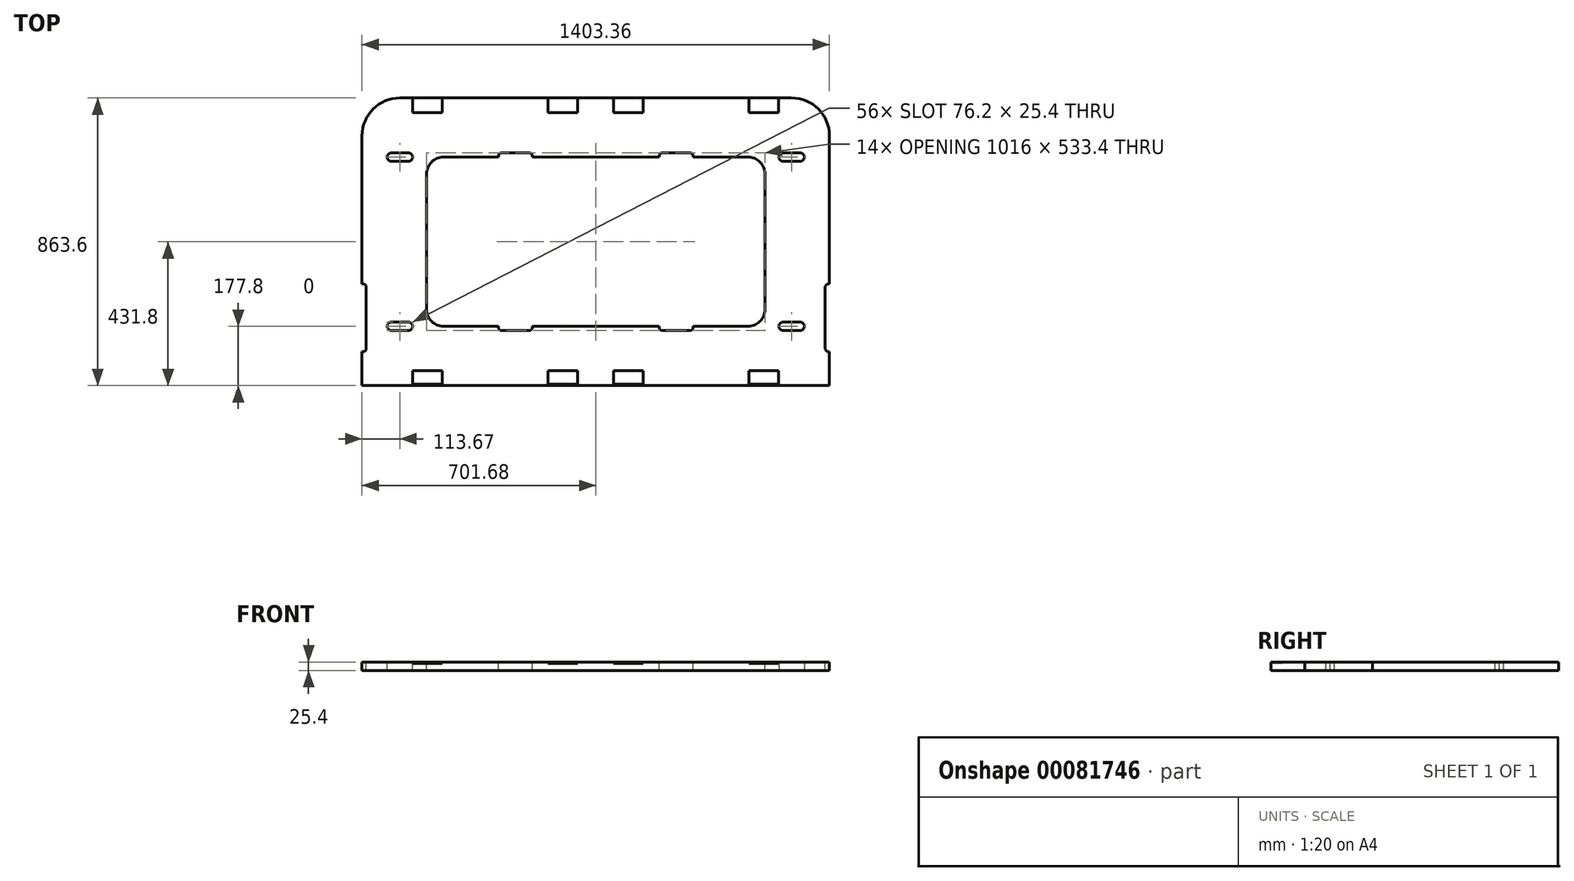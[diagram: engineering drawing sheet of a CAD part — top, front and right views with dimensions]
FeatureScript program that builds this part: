
annotation { "Feature Type Name" : "Feature", "Feature Type Description" : "" }
export const myFeature = defineFeature(function(context is Context, id is Id, definition is map)
    precondition{}
    {
        {
            var Q0;
            Q0=qCreatedBy(makeId("Top.planeOp"),FACE);
            var sketch = newSketch(context, id + "F0", { "sketchPlane" : qUnion([Q0])});
            skLineSegment(sketch, "E0.bottom", {"start": v(-701.68, -431.8) * mm, "end": v(701.68, -431.8) * mm});
            skLineSegment(sketch, "E0.top", {"start": v(-701.68, 431.8) * mm, "end": v(701.68, 431.8) * mm});
            skLineSegment(sketch, "E0.left", {"start": v(-701.68, -431.8) * mm, "end": v(-701.68, 431.8) * mm});
            skLineSegment(sketch, "E0.right", {"start": v(701.68, -431.8) * mm, "end": v(701.68, 431.8) * mm});
            skPoint(sketch, "E0.middle", {"position": v(0, 0) * mm});
            skSolve(sketch);
        }
        {
            var Q0;
            Q0=makeQuery(id+"F0.imprint","IMPRINT",FACE,{"disambiguationData":[TD([[makeQuery(id+"F0.imprint","IMPRINT",EDGE,{"derivedFrom":sQuery(id+"F0.wireOp",EDGE,"E0.bottom")}),1.0]])]});
            extrude(context, id + "F1", {"entities" : qUnion([Q0]), "depth" : 25.4 * mm, "offsetDistance" : 25.4 * mm});
        }
        {
            var Q0;
            Q0=makeQuery(id+"F1.opExtrude","CAP_FACE",FACE,{"disambiguationData":[OSD([sQuery(id+"F0.wireOp",EDGE,"E0.bottom"),sQuery(id+"F0.wireOp",EDGE,"E0.top"),sQuery(id+"F0.wireOp",EDGE,"E0.left"),sQuery(id+"F0.wireOp",EDGE,"E0.right")])],"isStart":false});
            var sketch = newSketch(context, id + "F2", { "sketchPlane" : qUnion([Q0])});
            skLineSegment(sketch, "E1.bottom", {"start": v(-457.2, 254) * mm, "end": v(457.2, 254) * mm});
            skLineSegment(sketch, "E1.top", {"start": v(-457.2, -254) * mm, "end": v(457.2, -254) * mm});
            skLineSegment(sketch, "E1.left", {"start": v(-508, 203.2) * mm, "end": v(-508, -203.2) * mm});
            skLineSegment(sketch, "E1.right", {"start": v(508, 203.2) * mm, "end": v(508, -203.2) * mm});
            skPoint(sketch, "E2.visualSharp", {"position": v(-508, 254) * mm});
            skArc(sketch, "E2.filletArc", {"start": v(-457.2, 254) * mm, "mid": v(-493.12, 239.12) * mm, "end": v(-508, 203.2) * mm});
            skPoint(sketch, "E3.visualSharp", {"position": v(508, 254) * mm});
            skArc(sketch, "E3.filletArc", {"start": v(508, 203.2) * mm, "mid": v(493.12, 239.12) * mm, "end": v(457.2, 254) * mm});
            skPoint(sketch, "E4.visualSharp", {"position": v(508, -254) * mm});
            skArc(sketch, "E4.filletArc", {"start": v(457.2, -254) * mm, "mid": v(493.12, -239.12) * mm, "end": v(508, -203.2) * mm});
            skPoint(sketch, "E5.visualSharp", {"position": v(-508, -254) * mm});
            skArc(sketch, "E5.filletArc", {"start": v(-508, -203.2) * mm, "mid": v(-493.12, -239.12) * mm, "end": v(-457.2, -254) * mm});
            skSolve(sketch);
        }
        {
            var Q0;
            Q0 = qSketchRegion(id + "F2", true);
            extrude(context, id + "F3", {"entities" : qUnion([Q0]), "operationType" : NewBodyOperationType.REMOVE, "oppositeDirection" : true, "depth" : 25.4 * mm});
        }
        {
            var Q0;
            Q0=makeQuery(id+"F1.opExtrude","CAP_FACE",FACE,{"disambiguationData":[OSD([sQuery(id+"F0.wireOp",EDGE,"E0.bottom"),sQuery(id+"F0.wireOp",EDGE,"E0.top"),sQuery(id+"F0.wireOp",EDGE,"E0.left"),sQuery(id+"F0.wireOp",EDGE,"E0.right")])],"isStart":false});
            var sketch = newSketch(context, id + "F4", { "sketchPlane" : qUnion([Q0])});
            skLineSegment(sketch, "E6.bottom", {"start": v(-549.27, -431.8) * mm, "end": v(-460.38, -431.8) * mm});
            skLineSegment(sketch, "E6.top", {"start": v(-549.27, -387.35) * mm, "end": v(-460.38, -387.35) * mm});
            skLineSegment(sketch, "E6.left", {"start": v(-549.27, -431.8) * mm, "end": v(-549.27, -387.35) * mm});
            skLineSegment(sketch, "E6.right", {"start": v(-460.37, -431.8) * mm, "end": v(-460.37, -387.35) * mm});
            skLineSegment(sketch, "E7.bottom", {"start": v(-142.87, -431.8) * mm, "end": v(-53.97, -431.8) * mm});
            skLineSegment(sketch, "E7.top", {"start": v(-142.87, -387.35) * mm, "end": v(-53.97, -387.35) * mm});
            skLineSegment(sketch, "E7.left", {"start": v(-142.87, -431.8) * mm, "end": v(-142.87, -387.35) * mm});
            skLineSegment(sketch, "E7.right", {"start": v(-53.97, -431.8) * mm, "end": v(-53.97, -387.35) * mm});
            skLineSegment(sketch, "E8.bottom", {"start": v(53.98, -431.8) * mm, "end": v(142.88, -431.8) * mm});
            skLineSegment(sketch, "E8.top", {"start": v(53.98, -387.35) * mm, "end": v(142.88, -387.35) * mm});
            skLineSegment(sketch, "E8.left", {"start": v(53.98, -431.8) * mm, "end": v(53.98, -387.35) * mm});
            skLineSegment(sketch, "E8.right", {"start": v(142.88, -431.8) * mm, "end": v(142.88, -387.35) * mm});
            skLineSegment(sketch, "E9.bottom", {"start": v(460.38, -431.8) * mm, "end": v(549.28, -431.8) * mm});
            skLineSegment(sketch, "E9.top", {"start": v(460.38, -387.35) * mm, "end": v(549.28, -387.35) * mm});
            skLineSegment(sketch, "E9.left", {"start": v(460.38, -431.8) * mm, "end": v(460.38, -387.35) * mm});
            skLineSegment(sketch, "E9.right", {"start": v(549.28, -431.8) * mm, "end": v(549.28, -387.35) * mm});
            skSolve(sketch);
        }
        {
            var Q0;
            Q0 = qSketchRegion(id + "F4", true);
            extrude(context, id + "F5", {"entities" : qUnion([Q0]), "operationType" : NewBodyOperationType.REMOVE, "oppositeDirection" : true, "depth" : 3.17 * mm});
        }
        {
            var Q0;
            Q0=makeQuery(id+"F1.opExtrude","CAP_FACE",FACE,{"disambiguationData":[OSD([sQuery(id+"F0.wireOp",EDGE,"E0.bottom"),sQuery(id+"F0.wireOp",EDGE,"E0.top"),sQuery(id+"F0.wireOp",EDGE,"E0.left"),sQuery(id+"F0.wireOp",EDGE,"E0.right")])],"isStart":false});
            var sketch = newSketch(context, id + "F6", { "sketchPlane" : qUnion([Q0])});
            skLineSegment(sketch, "E10.bottom", {"start": v(-549.27, -431.8) * mm, "end": v(-460.37, -431.8) * mm});
            skLineSegment(sketch, "E10.top", {"start": v(-549.27, -428) * mm, "end": v(-460.37, -428) * mm});
            skLineSegment(sketch, "E10.left", {"start": v(-549.27, -431.8) * mm, "end": v(-549.27, -428) * mm});
            skLineSegment(sketch, "E10.right", {"start": v(-460.37, -431.8) * mm, "end": v(-460.37, -428) * mm});
            skLineSegment(sketch, "E11.bottom", {"start": v(-142.87, -431.8) * mm, "end": v(-53.97, -431.8) * mm});
            skLineSegment(sketch, "E11.top", {"start": v(-142.87, -428) * mm, "end": v(-53.97, -428) * mm});
            skLineSegment(sketch, "E11.left", {"start": v(-142.87, -431.8) * mm, "end": v(-142.87, -428) * mm});
            skLineSegment(sketch, "E11.right", {"start": v(-53.97, -431.8) * mm, "end": v(-53.97, -428) * mm});
            skLineSegment(sketch, "E12.bottom", {"start": v(53.98, -431.8) * mm, "end": v(142.88, -431.8) * mm});
            skLineSegment(sketch, "E12.top", {"start": v(53.98, -428) * mm, "end": v(142.88, -428) * mm});
            skLineSegment(sketch, "E12.left", {"start": v(53.98, -431.8) * mm, "end": v(53.98, -428) * mm});
            skLineSegment(sketch, "E12.right", {"start": v(142.88, -431.8) * mm, "end": v(142.88, -428) * mm});
            skLineSegment(sketch, "E13.bottom", {"start": v(460.38, -431.8) * mm, "end": v(549.28, -431.8) * mm});
            skLineSegment(sketch, "E13.top", {"start": v(460.38, -428) * mm, "end": v(549.28, -428) * mm});
            skLineSegment(sketch, "E13.left", {"start": v(460.38, -431.8) * mm, "end": v(460.38, -428) * mm});
            skLineSegment(sketch, "E13.right", {"start": v(549.28, -431.8) * mm, "end": v(549.28, -428) * mm});
            skSolve(sketch);
        }
        {
            var Q0;
            Q0 = qSketchRegion(id + "F6", true);
            extrude(context, id + "F7", {"entities" : qUnion([Q0]), "operationType" : NewBodyOperationType.REMOVE, "oppositeDirection" : true, "depth" : 4.44 * mm});
        }
        {
            var Q0;
            Q0=makeQuery(id+"F1.opExtrude","SWEPT_EDGE",EDGE,{"disambiguationData":[OSD([sQuery(id+"F0.wireOp",EDGE,"E0.top"),sQuery(id+"F0.wireOp",EDGE,"E0.right")])]});
            var Q1;
            Q1=makeQuery(id+"F1.opExtrude","SWEPT_EDGE",EDGE,{"disambiguationData":[OSD([sQuery(id+"F0.wireOp",EDGE,"E0.top"),sQuery(id+"F0.wireOp",EDGE,"E0.left")])]});
            fillet(context, id + "F8", {"entities" : qUnion([Q0, Q1]), "radius" : 114.3 * mm, "tangentPropagation" : true, "allowEdgeOverflow" : false});
        }
        {
            var Q0;
            Q0=makeQuery(id+"F1.opExtrude","CAP_FACE",FACE,{"disambiguationData":[OSD([sQuery(id+"F0.wireOp",EDGE,"E0.bottom"),sQuery(id+"F0.wireOp",EDGE,"E0.top"),sQuery(id+"F0.wireOp",EDGE,"E0.left"),sQuery(id+"F0.wireOp",EDGE,"E0.right")])],"isStart":false});
            var sketch = newSketch(context, id + "F9", { "sketchPlane" : qUnion([Q0])});
            skLineSegment(sketch, "E14.bottom", {"start": v(53.97, 431.8) * mm, "end": v(142.88, 431.8) * mm});
            skLineSegment(sketch, "E14.top", {"start": v(53.97, 387.35) * mm, "end": v(142.88, 387.35) * mm});
            skLineSegment(sketch, "E14.left", {"start": v(53.97, 431.8) * mm, "end": v(53.97, 387.35) * mm});
            skLineSegment(sketch, "E14.right", {"start": v(142.87, 431.8) * mm, "end": v(142.87, 387.35) * mm});
            skLineSegment(sketch, "E15.bottom", {"start": v(460.38, 431.8) * mm, "end": v(549.28, 431.8) * mm});
            skLineSegment(sketch, "E15.top", {"start": v(460.38, 387.35) * mm, "end": v(549.28, 387.35) * mm});
            skLineSegment(sketch, "E15.left", {"start": v(460.38, 431.8) * mm, "end": v(460.38, 387.35) * mm});
            skLineSegment(sketch, "E15.right", {"start": v(549.28, 431.8) * mm, "end": v(549.28, 387.35) * mm});
            skLineSegment(sketch, "E16.bottom", {"start": v(-53.98, 431.8) * mm, "end": v(-142.88, 431.8) * mm});
            skLineSegment(sketch, "E16.top", {"start": v(-53.98, 387.35) * mm, "end": v(-142.88, 387.35) * mm});
            skLineSegment(sketch, "E16.left", {"start": v(-53.98, 431.8) * mm, "end": v(-53.98, 387.35) * mm});
            skLineSegment(sketch, "E16.right", {"start": v(-142.88, 431.8) * mm, "end": v(-142.88, 387.35) * mm});
            skLineSegment(sketch, "E17.bottom", {"start": v(-460.38, 431.8) * mm, "end": v(-549.28, 431.8) * mm});
            skLineSegment(sketch, "E17.top", {"start": v(-460.38, 387.35) * mm, "end": v(-549.28, 387.35) * mm});
            skLineSegment(sketch, "E17.left", {"start": v(-460.38, 431.8) * mm, "end": v(-460.38, 387.35) * mm});
            skLineSegment(sketch, "E17.right", {"start": v(-549.28, 431.8) * mm, "end": v(-549.28, 387.35) * mm});
            skSolve(sketch);
        }
        {
            var Q0;
            Q0 = qSketchRegion(id + "F9", true);
            extrude(context, id + "F10", {"entities" : qUnion([Q0]), "operationType" : NewBodyOperationType.REMOVE, "oppositeDirection" : true, "depth" : 3.17 * mm});
        }
        {
            var Q0;
            Q0=makeQuery(id+"F1.opExtrude","CAP_FACE",FACE,{"disambiguationData":[OSD([sQuery(id+"F0.wireOp",EDGE,"E0.bottom"),sQuery(id+"F0.wireOp",EDGE,"E0.top"),sQuery(id+"F0.wireOp",EDGE,"E0.left"),sQuery(id+"F0.wireOp",EDGE,"E0.right")])],"isStart":false});
            var sketch = newSketch(context, id + "F11", { "sketchPlane" : qUnion([Q0])});
            skLineSegment(sketch, "E18.bottom", {"start": v(-701.68, -127) * mm, "end": v(-688.98, -127) * mm});
            skLineSegment(sketch, "E18.top", {"start": v(-701.68, -330.2) * mm, "end": v(-688.98, -330.2) * mm});
            skLineSegment(sketch, "E18.left", {"start": v(-701.68, -127) * mm, "end": v(-701.68, -330.2) * mm});
            skLineSegment(sketch, "E18.right", {"start": v(-688.98, -127) * mm, "end": v(-688.98, -330.2) * mm});
            skLineSegment(sketch, "E19.bottom", {"start": v(701.68, -127) * mm, "end": v(688.98, -127) * mm});
            skLineSegment(sketch, "E19.top", {"start": v(701.68, -330.2) * mm, "end": v(688.98, -330.2) * mm});
            skLineSegment(sketch, "E19.left", {"start": v(701.68, -127) * mm, "end": v(701.68, -330.2) * mm});
            skLineSegment(sketch, "E19.right", {"start": v(688.98, -127) * mm, "end": v(688.98, -330.2) * mm});
            skSolve(sketch);
        }
        {
            var Q0;
            Q0 = qSketchRegion(id + "F11", true);
            extrude(context, id + "F12", {"entities" : qUnion([Q0]), "operationType" : NewBodyOperationType.REMOVE, "endBound" : BoundingType.THROUGH_ALL, "oppositeDirection" : true, "depth" : 25.4 * mm});
        }
        {
            var Q0;
            Q0=makeQuery(id+"F12.boolean.opBoolean","COPY",EDGE,{"derivedFrom":makeQuery(id+"F12.opExtrude","SWEPT_EDGE",EDGE,{"disambiguationData":[OSD([sQuery(id+"F11.wireOp",EDGE,"E18.bottom"),sQuery(id+"F11.wireOp",EDGE,"E18.right")])]})});
            var Q1;
            Q1=makeQuery(id+"F12.boolean.opBoolean","COPY",EDGE,{"derivedFrom":makeQuery(id+"F12.opExtrude","SWEPT_EDGE",EDGE,{"disambiguationData":[OSD([sQuery(id+"F11.wireOp",EDGE,"E18.top"),sQuery(id+"F11.wireOp",EDGE,"E18.right")])]})});
            var Q2;
            Q2=makeQuery(id+"F12.boolean.opBoolean","COPY",EDGE,{"derivedFrom":makeQuery(id+"F12.opExtrude","SWEPT_EDGE",EDGE,{"disambiguationData":[OSD([sQuery(id+"F11.wireOp",EDGE,"E19.bottom"),sQuery(id+"F11.wireOp",EDGE,"E19.right")])]})});
            var Q3;
            Q3=makeQuery(id+"F12.boolean.opBoolean","COPY",EDGE,{"derivedFrom":makeQuery(id+"F12.opExtrude","SWEPT_EDGE",EDGE,{"disambiguationData":[OSD([sQuery(id+"F11.wireOp",EDGE,"E19.top"),sQuery(id+"F11.wireOp",EDGE,"E19.right")])]})});
            fillet(context, id + "F13", {"entities" : qUnion([Q0, Q1, Q2, Q3]), "radius" : 9.52 * mm, "tangentPropagation" : true, "allowEdgeOverflow" : false});
        }
        {
            var Q0;
            Q0=makeQuery(id+"F1.opExtrude","CAP_FACE",FACE,{"disambiguationData":[OSD([sQuery(id+"F0.wireOp",EDGE,"E0.bottom"),sQuery(id+"F0.wireOp",EDGE,"E0.top"),sQuery(id+"F0.wireOp",EDGE,"E0.left"),sQuery(id+"F0.wireOp",EDGE,"E0.right")])],"isStart":false});
            var sketch = newSketch(context, id + "F14", { "sketchPlane" : qUnion([Q0])});
            skLineSegment(sketch, "E20.bottom", {"start": v(-292.1, -254) * mm, "end": v(-190.5, -254) * mm});
            skLineSegment(sketch, "E20.top", {"start": v(-292.1, -266.7) * mm, "end": v(-190.5, -266.7) * mm});
            skLineSegment(sketch, "E20.left", {"start": v(-292.1, -254) * mm, "end": v(-292.1, -266.7) * mm});
            skLineSegment(sketch, "E20.right", {"start": v(-190.5, -254) * mm, "end": v(-190.5, -266.7) * mm});
            skLineSegment(sketch, "E21.bottom", {"start": v(190.5, -254) * mm, "end": v(292.1, -254) * mm});
            skLineSegment(sketch, "E21.top", {"start": v(190.5, -266.7) * mm, "end": v(292.1, -266.7) * mm});
            skLineSegment(sketch, "E21.left", {"start": v(190.5, -254) * mm, "end": v(190.5, -266.7) * mm});
            skLineSegment(sketch, "E21.right", {"start": v(292.1, -254) * mm, "end": v(292.1, -266.7) * mm});
            skLineSegment(sketch, "E22.bottom", {"start": v(-292.1, 254) * mm, "end": v(-190.5, 254) * mm});
            skLineSegment(sketch, "E22.top", {"start": v(-292.1, 266.7) * mm, "end": v(-190.5, 266.7) * mm});
            skLineSegment(sketch, "E22.left", {"start": v(-292.1, 254) * mm, "end": v(-292.1, 266.7) * mm});
            skLineSegment(sketch, "E22.right", {"start": v(-190.5, 254) * mm, "end": v(-190.5, 266.7) * mm});
            skLineSegment(sketch, "E23.bottom", {"start": v(190.5, 254) * mm, "end": v(292.1, 254) * mm});
            skLineSegment(sketch, "E23.top", {"start": v(190.5, 266.7) * mm, "end": v(292.1, 266.7) * mm});
            skLineSegment(sketch, "E23.left", {"start": v(190.5, 254) * mm, "end": v(190.5, 266.7) * mm});
            skLineSegment(sketch, "E23.right", {"start": v(292.1, 254) * mm, "end": v(292.1, 266.7) * mm});
            skSolve(sketch);
        }
        {
            var Q0;
            Q0 = qSketchRegion(id + "F14", true);
            extrude(context, id + "F15", {"entities" : qUnion([Q0]), "operationType" : NewBodyOperationType.REMOVE, "endBound" : BoundingType.THROUGH_ALL, "oppositeDirection" : true, "depth" : 25.4 * mm});
        }
        {
            var Q0;
            Q0=makeQuery(id+"F15.boolean.opBoolean","COPY",EDGE,{"derivedFrom":makeQuery(id+"F15.opExtrude","SWEPT_EDGE",EDGE,{"disambiguationData":[OSD([sQuery(id+"F14.wireOp",EDGE,"E20.top"),sQuery(id+"F14.wireOp",EDGE,"E20.left")])]})});
            var Q1;
            Q1=makeQuery(id+"F15.boolean.opBoolean","COPY",EDGE,{"derivedFrom":makeQuery(id+"F15.opExtrude","SWEPT_EDGE",EDGE,{"disambiguationData":[OSD([sQuery(id+"F14.wireOp",EDGE,"E21.top"),sQuery(id+"F14.wireOp",EDGE,"E21.left")])]})});
            var Q2;
            Q2=makeQuery(id+"F15.boolean.opBoolean","COPY",EDGE,{"derivedFrom":makeQuery(id+"F15.opExtrude","SWEPT_EDGE",EDGE,{"disambiguationData":[OSD([sQuery(id+"F14.wireOp",EDGE,"E21.top"),sQuery(id+"F14.wireOp",EDGE,"E21.right")])]})});
            var Q3;
            Q3=makeQuery(id+"F15.boolean.opBoolean","COPY",EDGE,{"derivedFrom":makeQuery(id+"F15.opExtrude","SWEPT_EDGE",EDGE,{"disambiguationData":[OSD([sQuery(id+"F14.wireOp",EDGE,"E20.top"),sQuery(id+"F14.wireOp",EDGE,"E20.right")])]})});
            var Q4;
            Q4=makeQuery(id+"F15.boolean.opBoolean","COPY",EDGE,{"derivedFrom":makeQuery(id+"F15.opExtrude","SWEPT_EDGE",EDGE,{"disambiguationData":[OSD([sQuery(id+"F14.wireOp",EDGE,"E23.top"),sQuery(id+"F14.wireOp",EDGE,"E23.left")])]})});
            var Q5;
            Q5=makeQuery(id+"F15.boolean.opBoolean","COPY",EDGE,{"derivedFrom":makeQuery(id+"F15.opExtrude","SWEPT_EDGE",EDGE,{"disambiguationData":[OSD([sQuery(id+"F14.wireOp",EDGE,"E22.top"),sQuery(id+"F14.wireOp",EDGE,"E22.left")])]})});
            var Q6;
            Q6=makeQuery(id+"F15.boolean.opBoolean","COPY",EDGE,{"derivedFrom":makeQuery(id+"F15.opExtrude","SWEPT_EDGE",EDGE,{"disambiguationData":[OSD([sQuery(id+"F14.wireOp",EDGE,"E22.top"),sQuery(id+"F14.wireOp",EDGE,"E22.right")])]})});
            var Q7;
            Q7=makeQuery(id+"F15.boolean.opBoolean","COPY",EDGE,{"derivedFrom":makeQuery(id+"F15.opExtrude","SWEPT_EDGE",EDGE,{"disambiguationData":[OSD([sQuery(id+"F14.wireOp",EDGE,"E23.top"),sQuery(id+"F14.wireOp",EDGE,"E23.right")])]})});
            fillet(context, id + "F16", {"entities" : qUnion([Q0, Q1, Q2, Q3, Q4, Q5, Q6, Q7]), "radius" : 9.52 * mm, "tangentPropagation" : true, "allowEdgeOverflow" : false});
        }
        {
            var Q0;
            Q0=makeQuery(id+"F1.opExtrude","CAP_FACE",FACE,{"disambiguationData":[OSD([sQuery(id+"F0.wireOp",EDGE,"E0.bottom"),sQuery(id+"F0.wireOp",EDGE,"E0.top"),sQuery(id+"F0.wireOp",EDGE,"E0.left"),sQuery(id+"F0.wireOp",EDGE,"E0.right")])],"isStart":false});
            var sketch = newSketch(context, id + "F17", { "sketchPlane" : qUnion([Q0])});
            skLineSegment(sketch, "E24.bottom", {"start": v(-549.91, 241.3) * mm, "end": v(-626.11, 241.3) * mm});
            skLineSegment(sketch, "E24.top", {"start": v(-549.91, 266.7) * mm, "end": v(-626.11, 266.7) * mm});
            skLineSegment(sketch, "E24.left", {"start": v(-549.91, 241.3) * mm, "end": v(-549.91, 266.7) * mm});
            skLineSegment(sketch, "E24.right", {"start": v(-626.11, 241.3) * mm, "end": v(-626.11, 266.7) * mm});
            skLineSegment(sketch, "E25.bottom", {"start": v(549.9, 241.3) * mm, "end": v(626.1, 241.3) * mm});
            skLineSegment(sketch, "E25.top", {"start": v(549.9, 266.7) * mm, "end": v(626.1, 266.7) * mm});
            skLineSegment(sketch, "E25.left", {"start": v(549.9, 241.3) * mm, "end": v(549.9, 266.7) * mm});
            skLineSegment(sketch, "E25.right", {"start": v(626.1, 241.3) * mm, "end": v(626.1, 266.7) * mm});
            skLineSegment(sketch, "E26.bottom", {"start": v(549.91, -266.7) * mm, "end": v(626.11, -266.7) * mm});
            skLineSegment(sketch, "E26.top", {"start": v(549.91, -241.3) * mm, "end": v(626.11, -241.3) * mm});
            skLineSegment(sketch, "E26.left", {"start": v(549.91, -266.7) * mm, "end": v(549.91, -241.3) * mm});
            skLineSegment(sketch, "E26.right", {"start": v(626.11, -266.7) * mm, "end": v(626.11, -241.3) * mm});
            skLineSegment(sketch, "E27.bottom", {"start": v(-626.1, -241.3) * mm, "end": v(-549.9, -241.3) * mm});
            skLineSegment(sketch, "E27.top", {"start": v(-626.1, -266.7) * mm, "end": v(-549.9, -266.7) * mm});
            skLineSegment(sketch, "E27.left", {"start": v(-626.1, -241.3) * mm, "end": v(-626.1, -266.7) * mm});
            skLineSegment(sketch, "E27.right", {"start": v(-549.9, -241.3) * mm, "end": v(-549.9, -266.7) * mm});
            skSolve(sketch);
        }
        {
            var Q0;
            Q0 = qSketchRegion(id + "F17", true);
            extrude(context, id + "F18", {"entities" : qUnion([Q0]), "operationType" : NewBodyOperationType.REMOVE, "endBound" : BoundingType.THROUGH_ALL, "oppositeDirection" : true, "depth" : 25.4 * mm});
        }
        {
            var Q0;
            Q0=makeQuery(id+"F18.boolean.opBoolean","COPY",EDGE,{"derivedFrom":makeQuery(id+"F18.opExtrude","SWEPT_EDGE",EDGE,{"disambiguationData":[OSD([sQuery(id+"F17.wireOp",EDGE,"E24.bottom"),sQuery(id+"F17.wireOp",EDGE,"E24.right")])]})});
            var Q1;
            Q1=makeQuery(id+"F18.boolean.opBoolean","COPY",EDGE,{"derivedFrom":makeQuery(id+"F18.opExtrude","SWEPT_EDGE",EDGE,{"disambiguationData":[OSD([sQuery(id+"F17.wireOp",EDGE,"E24.bottom"),sQuery(id+"F17.wireOp",EDGE,"E24.left")])]})});
            var Q2;
            Q2=makeQuery(id+"F18.boolean.opBoolean","COPY",EDGE,{"derivedFrom":makeQuery(id+"F18.opExtrude","SWEPT_EDGE",EDGE,{"disambiguationData":[OSD([sQuery(id+"F17.wireOp",EDGE,"E24.top"),sQuery(id+"F17.wireOp",EDGE,"E24.left")])]})});
            var Q3;
            Q3=makeQuery(id+"F18.boolean.opBoolean","COPY",EDGE,{"derivedFrom":makeQuery(id+"F18.opExtrude","SWEPT_EDGE",EDGE,{"disambiguationData":[OSD([sQuery(id+"F17.wireOp",EDGE,"E24.top"),sQuery(id+"F17.wireOp",EDGE,"E24.right")])]})});
            var Q4;
            Q4=makeQuery(id+"F18.boolean.opBoolean","COPY",EDGE,{"derivedFrom":makeQuery(id+"F18.opExtrude","SWEPT_EDGE",EDGE,{"disambiguationData":[OSD([sQuery(id+"F17.wireOp",EDGE,"E27.bottom"),sQuery(id+"F17.wireOp",EDGE,"E27.left")])]})});
            var Q5;
            Q5=makeQuery(id+"F18.boolean.opBoolean","COPY",EDGE,{"derivedFrom":makeQuery(id+"F18.opExtrude","SWEPT_EDGE",EDGE,{"disambiguationData":[OSD([sQuery(id+"F17.wireOp",EDGE,"E27.top"),sQuery(id+"F17.wireOp",EDGE,"E27.left")])]})});
            var Q6;
            Q6=makeQuery(id+"F18.boolean.opBoolean","COPY",EDGE,{"derivedFrom":makeQuery(id+"F18.opExtrude","SWEPT_EDGE",EDGE,{"disambiguationData":[OSD([sQuery(id+"F17.wireOp",EDGE,"E27.top"),sQuery(id+"F17.wireOp",EDGE,"E27.right")])]})});
            var Q7;
            Q7=makeQuery(id+"F18.boolean.opBoolean","COPY",EDGE,{"derivedFrom":makeQuery(id+"F18.opExtrude","SWEPT_EDGE",EDGE,{"disambiguationData":[OSD([sQuery(id+"F17.wireOp",EDGE,"E27.bottom"),sQuery(id+"F17.wireOp",EDGE,"E27.right")])]})});
            var Q8;
            Q8=makeQuery(id+"F18.boolean.opBoolean","COPY",EDGE,{"derivedFrom":makeQuery(id+"F18.opExtrude","SWEPT_EDGE",EDGE,{"disambiguationData":[OSD([sQuery(id+"F17.wireOp",EDGE,"E26.top"),sQuery(id+"F17.wireOp",EDGE,"E26.right")])]})});
            var Q9;
            Q9=makeQuery(id+"F18.boolean.opBoolean","COPY",EDGE,{"derivedFrom":makeQuery(id+"F18.opExtrude","SWEPT_EDGE",EDGE,{"disambiguationData":[OSD([sQuery(id+"F17.wireOp",EDGE,"E26.bottom"),sQuery(id+"F17.wireOp",EDGE,"E26.right")])]})});
            var Q10;
            Q10=makeQuery(id+"F18.boolean.opBoolean","COPY",EDGE,{"derivedFrom":makeQuery(id+"F18.opExtrude","SWEPT_EDGE",EDGE,{"disambiguationData":[OSD([sQuery(id+"F17.wireOp",EDGE,"E26.bottom"),sQuery(id+"F17.wireOp",EDGE,"E26.left")])]})});
            var Q11;
            Q11=makeQuery(id+"F18.boolean.opBoolean","COPY",EDGE,{"derivedFrom":makeQuery(id+"F18.opExtrude","SWEPT_EDGE",EDGE,{"disambiguationData":[OSD([sQuery(id+"F17.wireOp",EDGE,"E26.top"),sQuery(id+"F17.wireOp",EDGE,"E26.left")])]})});
            var Q12;
            Q12=makeQuery(id+"F18.boolean.opBoolean","COPY",EDGE,{"derivedFrom":makeQuery(id+"F18.opExtrude","SWEPT_EDGE",EDGE,{"disambiguationData":[OSD([sQuery(id+"F17.wireOp",EDGE,"E25.top"),sQuery(id+"F17.wireOp",EDGE,"E25.left")])]})});
            var Q13;
            Q13=makeQuery(id+"F18.boolean.opBoolean","COPY",EDGE,{"derivedFrom":makeQuery(id+"F18.opExtrude","SWEPT_EDGE",EDGE,{"disambiguationData":[OSD([sQuery(id+"F17.wireOp",EDGE,"E25.bottom"),sQuery(id+"F17.wireOp",EDGE,"E25.left")])]})});
            var Q14;
            Q14=makeQuery(id+"F18.boolean.opBoolean","COPY",EDGE,{"derivedFrom":makeQuery(id+"F18.opExtrude","SWEPT_EDGE",EDGE,{"disambiguationData":[OSD([sQuery(id+"F17.wireOp",EDGE,"E25.bottom"),sQuery(id+"F17.wireOp",EDGE,"E25.right")])]})});
            var Q15;
            Q15=makeQuery(id+"F18.boolean.opBoolean","COPY",EDGE,{"derivedFrom":makeQuery(id+"F18.opExtrude","SWEPT_EDGE",EDGE,{"disambiguationData":[OSD([sQuery(id+"F17.wireOp",EDGE,"E25.top"),sQuery(id+"F17.wireOp",EDGE,"E25.right")])]})});
            fillet(context, id + "F19", {"entities" : qUnion([Q0, Q1, Q2, Q3, Q4, Q5, Q6, Q7, Q8, Q9, Q10, Q11, Q12, Q13, Q14, Q15]), "radius" : 12.7 * mm, "tangentPropagation" : true, "allowEdgeOverflow" : false});
        }
    });
